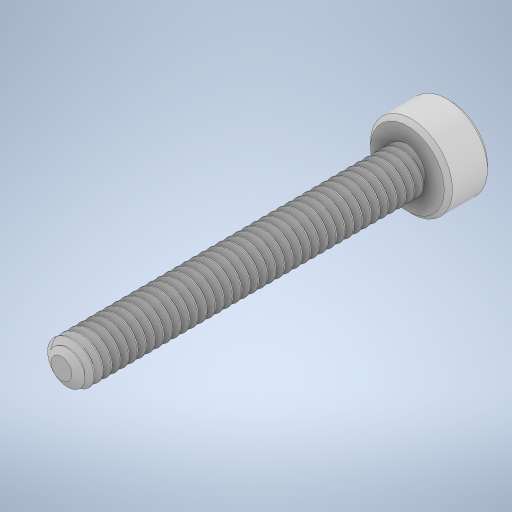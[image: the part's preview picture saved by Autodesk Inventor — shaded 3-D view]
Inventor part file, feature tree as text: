
AUTODESK INVENTOR PART (.ipt)
format: ipt  version: 2024 (Build 280153000, 153)  size: 1,227,264 bytes
history: native  units: mm
features: other x1, chamfer x1
ambient origin geometry x8: Origin, YZ Plane, XZ Plane, XY Plane, X Axis, Y Axis, Z Axis, Center Point
bodies: Body1 (feature_tree)
feature tree (2):
  other  "Těleso1"
  chamfer  "Chamfer1"  [1 undecoded]
note: 1 required parameter value undecoded (feature->parameter linkage not recoverable at this tier; creation-order binding heuristic only, values carry confidence <= 0.55)
